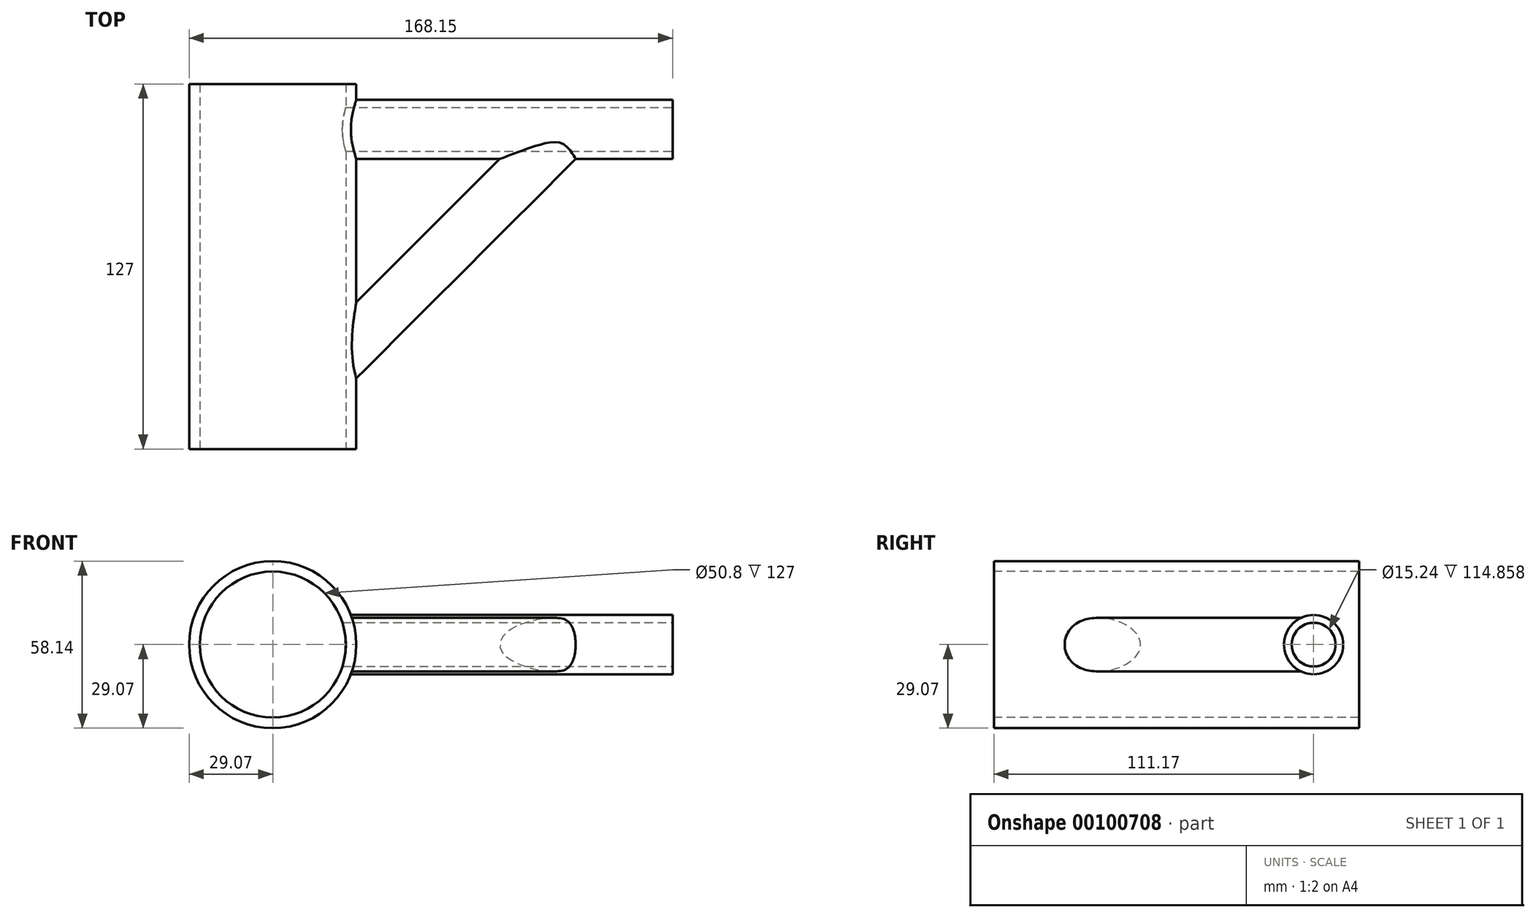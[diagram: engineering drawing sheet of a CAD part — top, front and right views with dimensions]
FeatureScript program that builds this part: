
annotation { "Feature Type Name" : "Feature", "Feature Type Description" : "" }
export const myFeature = defineFeature(function(context is Context, id is Id, definition is map)
    precondition{}
    {
        {
            var Q0;
            Q0=qCreatedBy(makeId("Front.planeOp"),FACE);
            var sketch = newSketch(context, id + "F0", { "sketchPlane" : qUnion([Q0])});
            skCircle(sketch, "E0", {"center": v(0, 0) * mm, "radius": 29.07 * mm});
            skSolve(sketch);
        }
        {
            var Q0;
            Q0 = qSketchRegion(id + "F0", true);
            extrude(context, id + "F1", {"entities" : qUnion([Q0]), "endBound" : BoundingType.SYMMETRIC, "depth" : 127 * mm});
        }
        {
            var Q0;
            Q0=makeQuery(id+"F1.opExtrude","CAP_FACE",FACE,{"disambiguationData":[OSD([sQuery(id+"F0.wireOp",EDGE,"E0")])],"isStart":false});
            var sketch = newSketch(context, id + "F2", { "sketchPlane" : qUnion([Q0])});
            skPoint(sketch, "E1", {"position": v(0, 0) * mm});
            skPoint(sketch, "E2", {"position": v(29.07, 0) * mm});
            skSolve(sketch);
        }
        {
            var Q0;
            Q0=sQuery(id+"F2.wireOp",VERTEX,"E1");
            var Q1;
            Q1=makeQuery(id+"F1.opExtrude","SWEPT_BODY",BODY,{"disambiguationData":[OSD([sQuery(id+"F0.wireOp",EDGE,"E0")])]});
            hole(context, id + "F3", {"style" : HoleStyle.SIMPLE, "endStyle" : HoleEndStyle.THROUGH, "holeDiameter" : 50.8 * mm, "locations" : qUnion([Q0]), "scope" : qUnion([Q1]), "isTappedThrough" : true});
        }
        {
            var Q0;
            Q0=makeQuery(id+"F1.opExtrude","CAP_FACE",FACE,{"disambiguationData":[OSD([sQuery(id+"F0.wireOp",EDGE,"E0")])],"isStart":false});
            var sketch = newSketch(context, id + "F4", { "sketchPlane" : qUnion([Q0])});
            skPoint(sketch, "E3", {"position": v(29.07, 0) * mm});
            skSolve(sketch);
        }
        {
            var Q0;
            Q0=sQuery(id+"F4.wireOp",VERTEX,"E3");
            var Q1;
            Q1=qCreatedBy(makeId("Right.planeOp"),FACE);
            cPlane(context, id + "F5", {"entities" : qUnion([Q0, Q1]), "cplaneType" : CPlaneType.PLANE_POINT, "offset" : 152.4 * mm, "width" : 152.4 * mm, "height" : 152.4 * mm});
        }
        {
            var Q0;
            Q0=qCreatedBy(id+"F5.planeOp",FACE);
            var sketch = newSketch(context, id + "F6", { "sketchPlane" : qUnion([Q0])});
            skCircle(sketch, "E4", {"center": v(47.67, 0) * mm, "radius": 10.3 * mm});
            skSolve(sketch);
        }
        {
            var Q0;
            Q0 = qSketchRegion(id + "F6", true);
            extrude(context, id + "F7", {"entities" : qUnion([Q0]), "operationType" : NewBodyOperationType.ADD, "depth" : 110.01 * mm, "hasSecondDirection" : true, "secondDirectionOppositeDirection" : true, "secondDirectionDepth" : 2.3 * mm});
        }
        {
            var Q0;
            Q0=makeQuery(id+"F4.imprint","IMPRINT",FACE,{"disambiguationData":[TD([[makeQuery(id+"F4.imprint","IMPRINT",EDGE,{"derivedFrom":makeQuery(id+"F1.opExtrude","CAP_EDGE",EDGE,{"disambiguationData":[OSD([sQuery(id+"F0.wireOp",EDGE,"E0")])],"isStart":false})}),1.0]])]});
            var sketch = newSketch(context, id + "F8", { "sketchPlane" : qUnion([Q0])});
            skLineSegment(sketch, "E5", {"start": v(30, 0) * mm, "end": v(30, 40.1) * mm});
            skSolve(sketch);
        }
        {
            var Q0;
            Q0=sQuery(id+"F8.wireOp",EDGE,"E5");
            cPlane(context, id + "F9", {"entities" : qUnion([Q0]), "cplaneType" : CPlaneType.LINE_ANGLE, "offset" : 152.4 * mm, "angle" : 45 * degree, "width" : 152.4 * mm, "height" : 152.4 * mm});
        }
        {
            var Q0;
            Q0=qCreatedBy(id+"F9.planeOp",FACE);
            var sketch = newSketch(context, id + "F10", { "sketchPlane" : qUnion([Q0])});
            skCircle(sketch, "E6", {"center": v(-38.75, 0) * mm, "radius": 9.32 * mm});
            skSolve(sketch);
        }
        {
            var Q0;
            Q0 = qSketchRegion(id + "F10", true);
            extrude(context, id + "F11", {"entities" : qUnion([Q0]), "operationType" : NewBodyOperationType.ADD, "depth" : 127 * mm, "hasSecondDirection" : true, "secondDirectionOppositeDirection" : false, "secondDirectionDepth" : 10.1 * mm});
        }
        {
            var Q0;
            Q0=makeQuery(id+"F7.opExtrude","CAP_FACE",FACE,{"disambiguationData":[OSD([sQuery(id+"F6.wireOp",EDGE,"E4")])],"isStart":false});
            var sketch = newSketch(context, id + "F12", { "sketchPlane" : qUnion([Q0])});
            skPoint(sketch, "E7", {"position": v(47.67, 0) * mm});
            skSolve(sketch);
        }
        {
            var Q0;
            Q0=sQuery(id+"F12.wireOp",VERTEX,"E7");
            var Q1;
            Q1=makeQuery(id+"F1.opExtrude","SWEPT_BODY",BODY,{"disambiguationData":[OSD([sQuery(id+"F0.wireOp",EDGE,"E0")])]});
            hole(context, id + "F13", {"style" : HoleStyle.SIMPLE, "endStyle" : HoleEndStyle.BLIND, "holeDiameter" : 15.24 * mm, "holeDepth" : 127 * mm, "locations" : qUnion([Q0]), "scope" : qUnion([Q1])});
        }
        {
            var Q0;
            Q0=qCreatedBy(makeId("Front.planeOp"),FACE);
            var sketch = newSketch(context, id + "F14", { "sketchPlane" : qUnion([Q0])});
            skCircle(sketch, "E8", {"center": v(0, 0) * mm, "radius": 25.4 * mm});
            skSolve(sketch);
        }
        {
            var Q0;
            Q0 = qSketchRegion(id + "F14", true);
            extrude(context, id + "F15", {"entities" : qUnion([Q0]), "operationType" : NewBodyOperationType.REMOVE, "depth" : 127 * mm});
        }
    });
